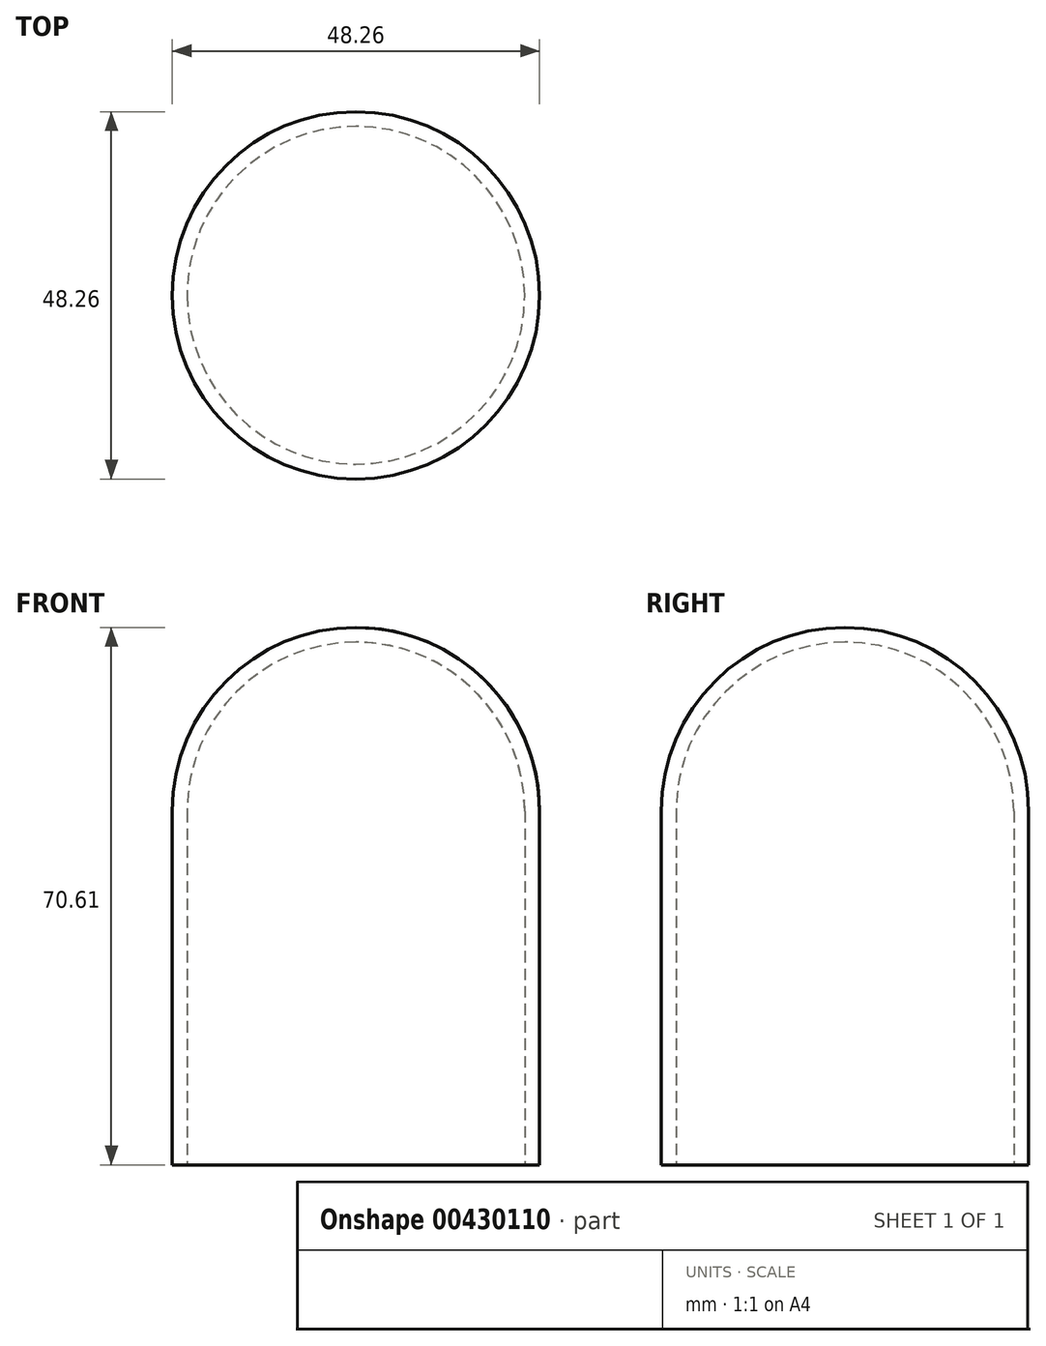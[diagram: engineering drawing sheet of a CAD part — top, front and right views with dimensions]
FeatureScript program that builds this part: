
annotation { "Feature Type Name" : "Feature", "Feature Type Description" : "" }
export const myFeature = defineFeature(function(context is Context, id is Id, definition is map)
    precondition{}
    {
        {
            var Q0;
            Q0=qCreatedBy(makeId("Top.planeOp"),FACE);
            var sketch = newSketch(context, id + "F0", { "sketchPlane" : qUnion([Q0])});
            skCircle(sketch, "E0", {"center": v(0, 0) * mm, "radius": 24.13 * mm});
            skSolve(sketch);
        }
        {
            var Q0;
            Q0=makeQuery(id+"F0.imprint","IMPRINT",FACE,{"disambiguationData":[TD([[makeQuery(id+"F0.imprint","IMPRINT",EDGE,{"derivedFrom":sQuery(id+"F0.wireOp",EDGE,"E0")}),1.0]])]});
            extrude(context, id + "F1", {"entities" : qUnion([Q0]), "depth" : 70.61 * mm});
        }
        {
            var Q0;
            Q0=makeQuery(id+"F1.opExtrude","CAP_EDGE",EDGE,{"disambiguationData":[OSD([sQuery(id+"F0.wireOp",EDGE,"E0")])],"isStart":false});
            fillet(context, id + "F2", {"entities" : qUnion([Q0]), "radius" : 24.13 * mm, "tangentPropagation" : true, "allowEdgeOverflow" : false});
        }
        {
            var Q0;
            Q0=makeQuery(id+"F1.opExtrude","CAP_FACE",FACE,{"disambiguationData":[OSD([sQuery(id+"F0.wireOp",EDGE,"E0")])],"isStart":false});
            var sketch = newSketch(context, id + "F3", { "sketchPlane" : qUnion([Q0])});
            skSolve(sketch);
        }
        {
            var Q0;
            Q0=makeQuery(id+"F1.opExtrude","CAP_FACE",FACE,{"disambiguationData":[OSD([sQuery(id+"F0.wireOp",EDGE,"E0")])],"isStart":true});
            var Q1;
            Q1=makeQuery(id+"F1.opExtrude","CAP_FACE",FACE,{"disambiguationData":[OSD([sQuery(id+"F0.wireOp",EDGE,"E0")])],"isStart":false});
            shell(context, id + "F4", {"entities" : qUnion([Q0, Q1]), "thickness" : 1.94 * mm});
        }
    });
